# Revit family: EP-945
name_source: partatom
category: Aparatos sanitarios
units: mm (PartAtom-declared; Revit-internal decimal feet)

## family parameters
Compartido = No
Corte con vacíos al cargar = No
Cota de conector redondo = Diámetro de uso
Número OmniClass = 23.45.00.00
Punto de cálculo de habitación = No
Se basa en plano de trabajo = No
Siempre vertical = Sí
Tipo de pieza = Normal
Título OmniClass = Sanitary, Laundry, and Cleaning Equipment

## types (1)
- EP-945
    Brass Chromed = Brass
    Comentarios de tipo = Monomando mediano de lavabo. Incluye contra de push. Incluye inserto para usarse con lavabos sin rebosadero.
    Data Sheet = https://helvex.com.mx
    Descripción = Monomando medio para lavabo con contra de push.
    Elevación por defecto = 35"
    Fabricante = HELVEX
    Inlet Threads = ½" - 14 NPSM
    Instructive = https://helvex.com.mx
    Max. Working Pressure = 85.3 psi
    Min. Working Pressure = 3.6 psi
    Modelo = EP-945
    Total Diameter = 2"
    Total Height = 14"
    Total Length = 9"
    URL = https://helvex.com.mx

## geometry (parser evidence)
native form markers: Sweep x3
no freeform markers — native parametric forms only
